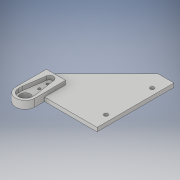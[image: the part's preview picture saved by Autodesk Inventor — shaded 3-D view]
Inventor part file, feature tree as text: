
AUTODESK INVENTOR PART (.ipt)
format: ipt  version: 2017 (Build 210142000, 142)  size: 159,744 bytes
history: native  units: in
note: dims shown in document units (in); Inventor stores cm internally (conversion verified against a paired STEP export)
features: extrude x2, sketch x2, projected_geometry x1
ambient origin geometry x8: Origin, YZ Plane, XZ Plane, XY Plane, X Axis, Y Axis, Z Axis, Center Point
bodies: Solid1 (feature_tree)
feature tree (5):
  extrude  "Extrusion1"  TaperAngle=90.0deg  [1 undecoded]
  extrude  "Extrusion3"  Depth=1.6142in
  sketch  "Sketch3"  dims[d6=2.3622in d7=90.0deg]
  sketch  "Sketch6"  dims[d8=0.4929in d9=1.6142in d10=0.2953in d11=0.5906in d13=0.9456in d14=0.1181in d15=0.0in d18=0.1969in d19=0.4724in d20=0.4724in d21=0.1181in d22=0.1181in d25=0.315in d26=0.4335in d27=0.2562in d28=0.0787in d29=0.0787in d31=0.4331in d32=0.0591in d33=0.2362in d34=0.1181in d35=0.1181in d36=0.0in]
  projected_geometry  "Projected Loop3"
note: 1 required parameter value undecoded (feature->parameter linkage not recoverable at this tier; creation-order binding heuristic only, values carry confidence <= 0.55)
